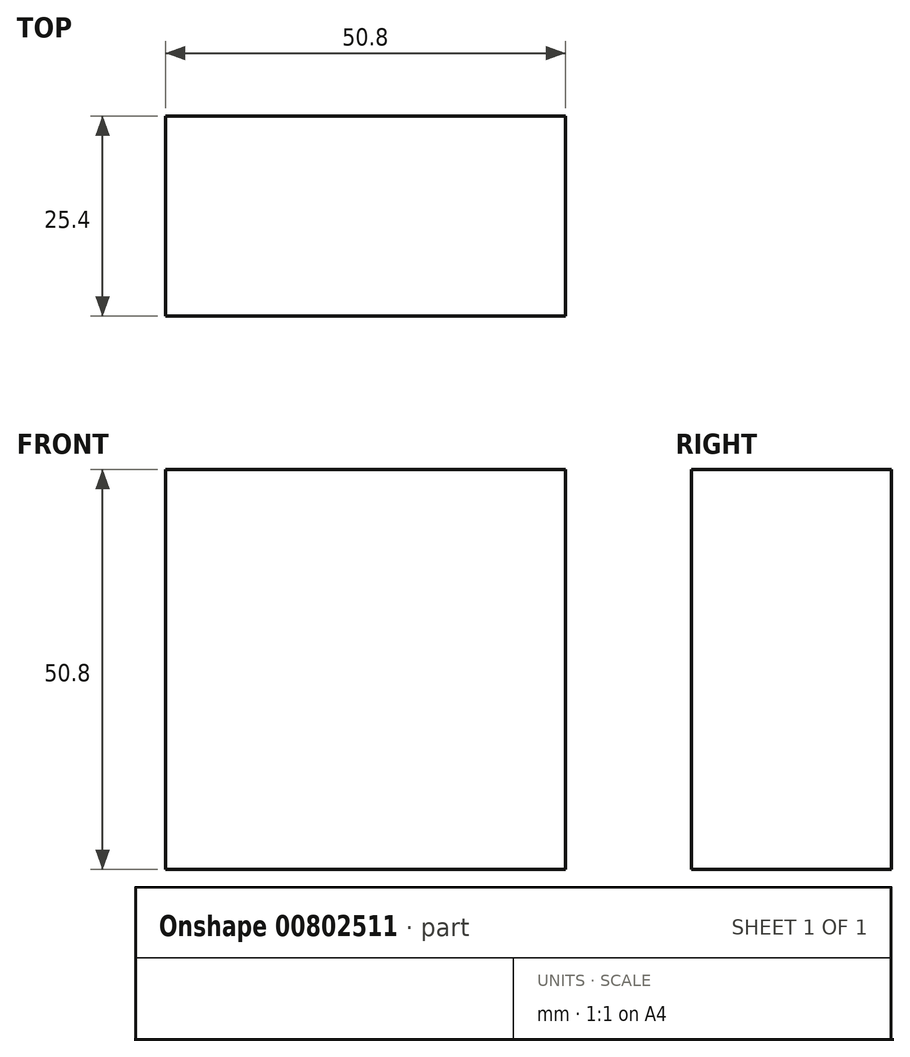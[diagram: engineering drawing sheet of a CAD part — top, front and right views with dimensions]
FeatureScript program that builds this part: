
annotation { "Feature Type Name" : "Feature", "Feature Type Description" : "" }
export const myFeature = defineFeature(function(context is Context, id is Id, definition is map)
    precondition{}
    {
        {
            var Q0;
            Q0=qCreatedBy(makeId("Front.planeOp"),FACE);
            var sketch = newSketch(context, id + "F0", { "sketchPlane" : qUnion([Q0])});
            skLineSegment(sketch, "E0.bottom", {"start": v(-25.4, 25.4) * mm, "end": v(25.4, 25.4) * mm});
            skLineSegment(sketch, "E0.top", {"start": v(-25.4, -25.4) * mm, "end": v(25.4, -25.4) * mm});
            skLineSegment(sketch, "E0.left", {"start": v(-25.4, 25.4) * mm, "end": v(-25.4, -25.4) * mm});
            skLineSegment(sketch, "E0.right", {"start": v(25.4, 25.4) * mm, "end": v(25.4, -25.4) * mm});
            skPoint(sketch, "E0.middle", {"position": v(0, 0) * mm});
            skSolve(sketch);
        }
        {
            var Q0;
            Q0 = qSketchRegion(id + "F0", true);
            extrude(context, id + "F1", {"entities" : qUnion([Q0]), "depth" : 25.4 * mm, "offsetDistance" : 25.4 * mm});
        }
    });
